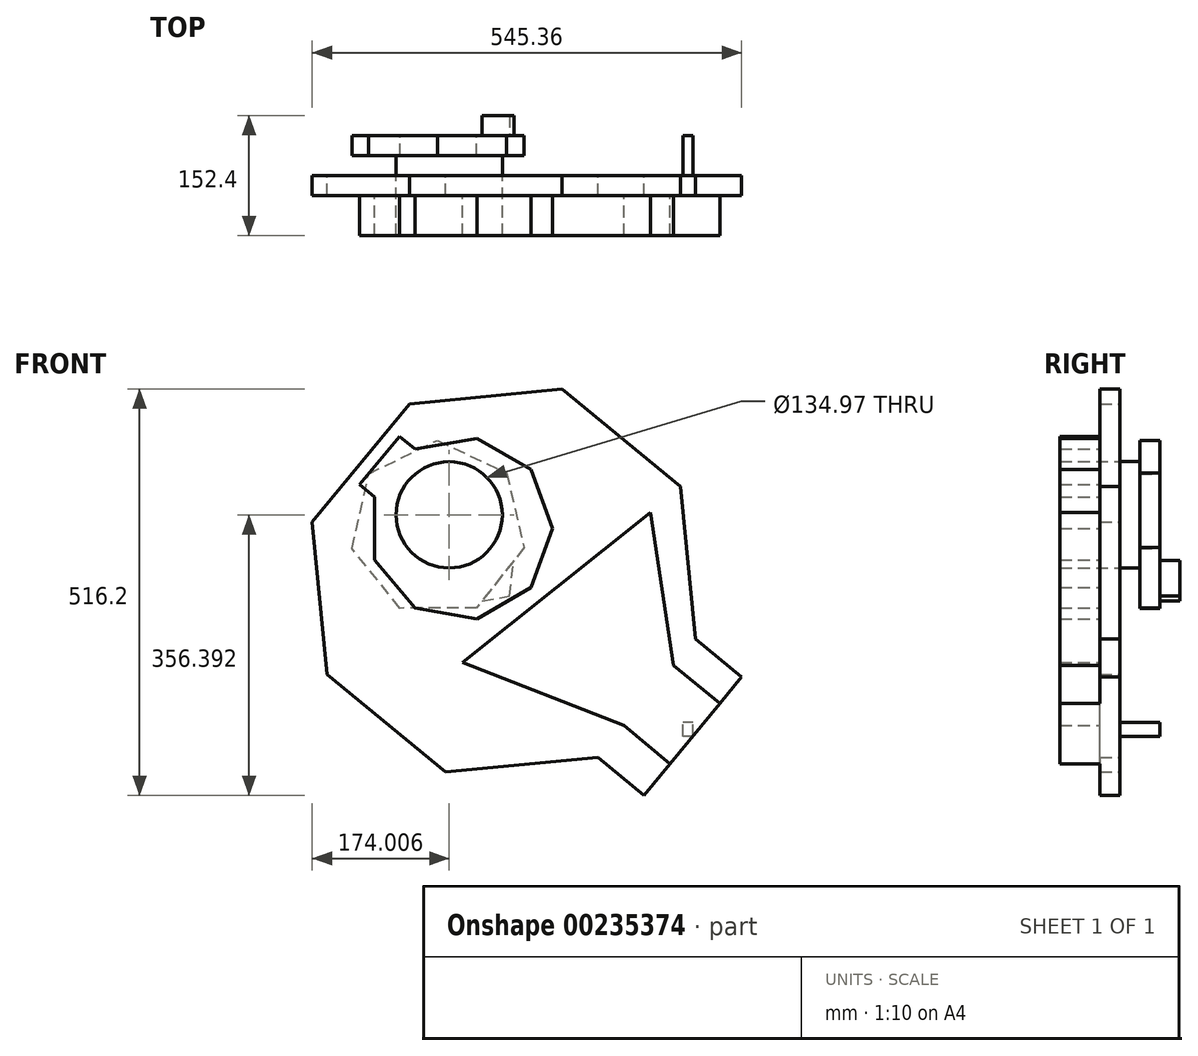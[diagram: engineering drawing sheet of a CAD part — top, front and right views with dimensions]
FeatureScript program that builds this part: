
annotation { "Feature Type Name" : "Feature", "Feature Type Description" : "" }
export const myFeature = defineFeature(function(context is Context, id is Id, definition is map)
    precondition{}
    {
        {
            var Q0;
            Q0=qCreatedBy(makeId("Front.planeOp"),FACE);
            var sketch = newSketch(context, id + "F0", { "sketchPlane" : qUnion([Q0])});
            skLineSegment(sketch, "E0.bottom", {"start": v(0, 0) * mm, "end": v(42.08, 0) * mm});
            skLineSegment(sketch, "E0.top", {"start": v(0, 55.56) * mm, "end": v(42.08, 55.56) * mm});
            skLineSegment(sketch, "E0.left", {"start": v(0, 0) * mm, "end": v(0, 55.56) * mm});
            skLineSegment(sketch, "E0.right", {"start": v(42.08, 0) * mm, "end": v(42.08, 55.56) * mm});
            skSolve(sketch);
        }
        {
            var Q0;
            Q0 = qSketchRegion(id + "F0", true);
            extrude(context, id + "F1", {"entities" : qUnion([Q0]), "depth" : 25.4 * mm});
        }
        {
            var Q0;
            Q0=makeQuery(id+"F1.opExtrude","CAP_FACE",FACE,{"disambiguationData":[OSD([sQuery(id+"F0.wireOp",EDGE,"E0.bottom"),sQuery(id+"F0.wireOp",EDGE,"E0.top"),sQuery(id+"F0.wireOp",EDGE,"E0.left"),sQuery(id+"F0.wireOp",EDGE,"E0.right")])],"isStart":false});
            var sketch = newSketch(context, id + "F2", { "sketchPlane" : qUnion([Q0])});
            skCircle(sketch, "E1", {"center": v(14.29, 17.4) * mm, "radius": 67.49 * mm});
            skSolve(sketch);
        }
        {
            var Q0;
            Q0 = qSketchRegion(id + "F2", true);
            extrude(context, id + "F3", {"entities" : qUnion([Q0]), "operationType" : NewBodyOperationType.ADD, "depth" : 25.4 * mm});
        }
        {
            var Q0;
            Q0=qCreatedBy(makeId("Front.planeOp"),FACE);
            var sketch = newSketch(context, id + "F4", { "sketchPlane" : qUnion([Q0])});
            skCircle(sketch, "E2.cCircle", {"center": v(0, 0) * mm, "radius": 100.97 * mm, "construction": true});
            skLineSegment(sketch, "E2.0", {"start": v(-48.02, -101.27) * mm, "end": v(-109.11, -25.6) * mm});
            skLineSegment(sketch, "E2.1", {"start": v(-109.11, -25.6) * mm, "end": v(-88.04, 69.35) * mm});
            skLineSegment(sketch, "E2.2", {"start": v(-88.04, 69.35) * mm, "end": v(-0.68, 112.07) * mm});
            skLineSegment(sketch, "E2.3", {"start": v(-0.68, 112.07) * mm, "end": v(87.2, 70.4) * mm});
            skLineSegment(sketch, "E2.4", {"start": v(87.2, 70.4) * mm, "end": v(109.41, -24.28) * mm});
            skLineSegment(sketch, "E2.5", {"start": v(109.41, -24.28) * mm, "end": v(49.24, -100.68) * mm});
            skLineSegment(sketch, "E2.6", {"start": v(49.24, -100.68) * mm, "end": v(-48.02, -101.27) * mm});
            skPoint(sketch, "E2.0.midPoint", {"position": v(-78.56, -63.43) * mm});
            skSolve(sketch);
        }
        {
            var Q0;
            Q0=makeQuery(id+"F4.imprint","IMPRINT",FACE,{"disambiguationData":[TD([[makeQuery(id+"F4.imprint","IMPRINT",EDGE,{"derivedFrom":sQuery(id+"F4.wireOp",EDGE,"E2.0")}),-1.0]])]});
            extrude(context, id + "F5", {"entities" : qUnion([Q0]), "operationType" : NewBodyOperationType.ADD, "depth" : 25.4 * mm});
        }
        {
            var Q0;
            Q0=makeQuery(id+"F3.opExtrude","CAP_FACE",FACE,{"disambiguationData":[OSD([sQuery(id+"F2.wireOp",EDGE,"E1")])],"isStart":false});
            var sketch = newSketch(context, id + "F6", { "sketchPlane" : qUnion([Q0])});
            skCircle(sketch, "E3.cCircle", {"center": v(83.55, -66.06) * mm, "radius": 234.98 * mm, "construction": true});
            skLineSegment(sketch, "E3.0", {"start": v(-35.98, 158.44) * mm, "end": v(157.78, 177.2) * mm});
            skLineSegment(sketch, "E3.1", {"start": v(157.78, 177.2) * mm, "end": v(308.05, 53.46) * mm});
            skLineSegment(sketch, "E3.2", {"start": v(308.05, 53.46) * mm, "end": v(326.81, -140.3) * mm});
            skLineSegment(sketch, "E3.3", {"start": v(326.81, -140.3) * mm, "end": v(203.07, -290.57) * mm});
            skLineSegment(sketch, "E3.4", {"start": v(203.07, -290.57) * mm, "end": v(9.32, -309.33) * mm});
            skLineSegment(sketch, "E3.5", {"start": v(9.32, -309.33) * mm, "end": v(-140.96, -185.58) * mm});
            skLineSegment(sketch, "E3.6", {"start": v(-140.96, -185.58) * mm, "end": v(-159.72, 8.17) * mm});
            skLineSegment(sketch, "E3.7", {"start": v(-159.72, 8.17) * mm, "end": v(-35.98, 158.44) * mm});
            skPoint(sketch, "E3.0.midPoint", {"position": v(60.9, 167.82) * mm});
            skSolve(sketch);
        }
        {
            var Q0;
            Q0=makeQuery(id+"F6.imprint","IMPRINT",FACE,{"disambiguationData":[TD([[makeQuery(id+"F6.imprint","IMPRINT",EDGE,{"derivedFrom":sQuery(id+"F6.wireOp",EDGE,"E3.0")}),-1.0]])]});
            extrude(context, id + "F7", {"entities" : qUnion([Q0]), "depth" : 25.4 * mm});
        }
        {
            var Q0;
            Q0=makeQuery(id+"F7.opExtrude","CAP_FACE",FACE,{"disambiguationData":[OSD([sQuery(id+"F2.wireOp",EDGE,"E1"),sQuery(id+"F6.wireOp",EDGE,"E3.0"),sQuery(id+"F6.wireOp",EDGE,"E3.1"),sQuery(id+"F6.wireOp",EDGE,"E3.2"),sQuery(id+"F6.wireOp",EDGE,"E3.3"),sQuery(id+"F6.wireOp",EDGE,"E3.4"),sQuery(id+"F6.wireOp",EDGE,"E3.5"),sQuery(id+"F6.wireOp",EDGE,"E3.6"),sQuery(id+"F6.wireOp",EDGE,"E3.7")])],"isStart":false});
            var sketch = newSketch(context, id + "F8", { "sketchPlane" : qUnion([Q0])});
            skCircle(sketch, "E4.cCircle", {"center": v(205.53, -143.68) * mm, "radius": 176.31 * mm, "construction": true});
            skLineSegment(sketch, "E4.0", {"start": v(315.67, -281.36) * mm, "end": v(31.23, -170.23) * mm});
            skLineSegment(sketch, "E4.1", {"start": v(31.23, -170.23) * mm, "end": v(269.7, 20.54) * mm});
            skLineSegment(sketch, "E4.2", {"start": v(269.7, 20.54) * mm, "end": v(315.67, -281.36) * mm});
            skSolve(sketch);
        }
        {
            var Q0;
            {var subQ0=sQuery(id+"F8.wireOp",EDGE,"E4.1");Q0=makeQuery(id+"F8.imprint","IMPRINT",FACE,{"disambiguationData":[TD([[makeQuery(id+"F8.imprint","IMPRINT",EDGE,{"derivedFrom":subQ0}),-1.0]])]});}
            extrude(context, id + "F9", {"entities" : qUnion([Q0]), "operationType" : NewBodyOperationType.ADD, "depth" : 25.4 * mm});
        }
        {
            var Q0;
            Q0=makeQuery(id+"F7.opExtrude","CAP_FACE",FACE,{"disambiguationData":[OSD([sQuery(id+"F2.wireOp",EDGE,"E1"),sQuery(id+"F6.wireOp",EDGE,"E3.0"),sQuery(id+"F6.wireOp",EDGE,"E3.1"),sQuery(id+"F6.wireOp",EDGE,"E3.2"),sQuery(id+"F6.wireOp",EDGE,"E3.3"),sQuery(id+"F6.wireOp",EDGE,"E3.4"),sQuery(id+"F6.wireOp",EDGE,"E3.5"),sQuery(id+"F6.wireOp",EDGE,"E3.6"),sQuery(id+"F6.wireOp",EDGE,"E3.7")])],"isStart":false});
            var sketch = newSketch(context, id + "F10", { "sketchPlane" : qUnion([Q0])});
            skCircle(sketch, "E5.cCircle", {"center": v(29.15, 0) * mm, "radius": 109.38 * mm, "construction": true});
            skLineSegment(sketch, "E5.0", {"start": v(-80.23, -39.81) * mm, "end": v(-80.23, 39.81) * mm});
            skLineSegment(sketch, "E5.1", {"start": v(-80.23, 39.81) * mm, "end": v(-29.05, 100.8) * mm});
            skLineSegment(sketch, "E5.2", {"start": v(-29.05, 100.8) * mm, "end": v(49.36, 114.63) * mm});
            skLineSegment(sketch, "E5.3", {"start": v(49.36, 114.63) * mm, "end": v(118.31, 74.82) * mm});
            skLineSegment(sketch, "E5.4", {"start": v(118.31, 74.82) * mm, "end": v(145.55, 0) * mm});
            skLineSegment(sketch, "E5.5", {"start": v(145.55, 0) * mm, "end": v(118.31, -74.82) * mm});
            skLineSegment(sketch, "E5.6", {"start": v(118.31, -74.82) * mm, "end": v(49.36, -114.63) * mm});
            skLineSegment(sketch, "E5.7", {"start": v(49.36, -114.63) * mm, "end": v(-29.05, -100.8) * mm});
            skLineSegment(sketch, "E5.8", {"start": v(-29.05, -100.8) * mm, "end": v(-80.23, -39.81) * mm});
            skPoint(sketch, "E5.0.midPoint", {"position": v(-80.23, 0) * mm});
            skSolve(sketch);
        }
        {
            var Q0;
            Q0=makeQuery(id+"F10.imprint","IMPRINT",FACE,{"disambiguationData":[TD([[makeQuery(id+"F10.imprint","IMPRINT",EDGE,{"derivedFrom":sQuery(id+"F10.wireOp",EDGE,"E5.0")}),-1.0]])]});
            extrude(context, id + "F11", {"entities" : qUnion([Q0]), "operationType" : NewBodyOperationType.ADD, "depth" : 25.4 * mm});
        }
        {
            var Q0;
            Q0=makeQuery(id+"F11.opExtrude","SWEPT_FACE",FACE,{"disambiguationData":[OSD([sQuery(id+"F10.wireOp",EDGE,"E5.1")])]});
            extrude(context, id + "F12", {"entities" : qUnion([Q0]), "operationType" : NewBodyOperationType.ADD, "depth" : 25.4 * mm});
        }
        {
            var Q0;
            {var subQ0=sQuery(id+"F10.wireOp",EDGE,"E5.1");Q0=makeQuery(id+"F12.boolean.opBoolean","MERGE",FACE,{"derivedFrom":[makeQuery(id+"F11.opExtrude","CAP_FACE",FACE,{"disambiguationData":[OSD([sQuery(id+"F2.wireOp",EDGE,"E1"),sQuery(id+"F10.wireOp",EDGE,"E5.0"),subQ0,sQuery(id+"F10.wireOp",EDGE,"E5.2"),sQuery(id+"F10.wireOp",EDGE,"E5.3"),sQuery(id+"F10.wireOp",EDGE,"E5.4"),sQuery(id+"F10.wireOp",EDGE,"E5.5"),sQuery(id+"F10.wireOp",EDGE,"E5.6"),sQuery(id+"F10.wireOp",EDGE,"E5.7"),sQuery(id+"F10.wireOp",EDGE,"E5.8")])],"isStart":false}),makeQuery(id+"F12.opExtrude","SWEPT_FACE",FACE,{"disambiguationData":[OSD([subQ0]),TDD([makeQuery(id+"F11.opExtrude","CAP_EDGE",EDGE,{"disambiguationData":[OSD([subQ0])],"isStart":false})])]})]});}
            var Q1;
            Q1=makeQuery(id+"F9.opExtrude","CAP_FACE",FACE,{"disambiguationData":[OSD([sQuery(id+"F6.wireOp",EDGE,"E3.3"),sQuery(id+"F8.wireOp",EDGE,"E4.0"),sQuery(id+"F8.wireOp",EDGE,"E4.1"),sQuery(id+"F8.wireOp",EDGE,"E4.2")])],"isStart":false});
            extrude(context, id + "F13", {"entities" : qUnion([Q0, Q1]), "operationType" : NewBodyOperationType.ADD, "depth" : 25.4 * mm});
        }
        {
            var Q0;
            {var subQ0=sQuery(id+"F6.wireOp",EDGE,"E3.3");Q0=makeQuery(id+"F13.boolean.opBoolean","MERGE",FACE,{"derivedFrom":[makeQuery(id+"F9.boolean.opBoolean","MERGE",FACE,{"derivedFrom":[makeQuery(id+"F7.opExtrude","SWEPT_FACE",FACE,{"disambiguationData":[OSD([subQ0])]}),makeQuery(id+"F9.opExtrude","SWEPT_FACE",FACE,{"disambiguationData":[OSD([subQ0])]})]}),makeQuery(id+"F13.opExtrude","SWEPT_FACE",FACE,{"disambiguationData":[OSD([subQ0])]})]});}
            extrude(context, id + "F14", {"entities" : qUnion([Q0]), "operationType" : NewBodyOperationType.ADD, "depth" : 25.4 * mm});
        }
        {
            var Q0;
            Q0=makeQuery(id+"F14.opExtrude","CAP_FACE",FACE,{"disambiguationData":[OSD([sQuery(id+"F6.wireOp",EDGE,"E3.3")])],"isStart":false});
            extrude(context, id + "F15", {"entities" : qUnion([Q0]), "operationType" : NewBodyOperationType.ADD, "depth" : 25.4 * mm});
        }
        {
            var Q0;
            Q0=makeQuery(id+"F15.opExtrude","CAP_FACE",FACE,{"disambiguationData":[OSD([sQuery(id+"F6.wireOp",EDGE,"E3.3")])],"isStart":false});
            extrude(context, id + "F16", {"entities" : qUnion([Q0]), "operationType" : NewBodyOperationType.ADD, "depth" : 25.4 * mm});
        }
        {
            var Q0;
            {var subQ0=sQuery(id+"F6.wireOp",EDGE,"E3.3");var subQ1=makeQuery(id+"F7.opExtrude","CAP_EDGE",EDGE,{"disambiguationData":[OSD([subQ0])],"isStart":true});var subQ2=makeQuery(id+"F14.opExtrude","CAP_EDGE",EDGE,{"disambiguationData":[OSD([subQ0]),TDD([subQ1])],"isStart":false});Q0=makeQuery(id+"F16.boolean.opBoolean","MERGE",FACE,{"derivedFrom":[makeQuery(id+"F15.boolean.opBoolean","MERGE",FACE,{"derivedFrom":[makeQuery(id+"F14.boolean.opBoolean","MERGE",FACE,{"derivedFrom":[makeQuery(id+"F7.opExtrude","CAP_FACE",FACE,{"disambiguationData":[OSD([sQuery(id+"F2.wireOp",EDGE,"E1"),sQuery(id+"F6.wireOp",EDGE,"E3.0"),sQuery(id+"F6.wireOp",EDGE,"E3.1"),sQuery(id+"F6.wireOp",EDGE,"E3.2"),subQ0,sQuery(id+"F6.wireOp",EDGE,"E3.4"),sQuery(id+"F6.wireOp",EDGE,"E3.5"),sQuery(id+"F6.wireOp",EDGE,"E3.6"),sQuery(id+"F6.wireOp",EDGE,"E3.7")])],"isStart":true}),makeQuery(id+"F14.opExtrude","SWEPT_FACE",FACE,{"disambiguationData":[OSD([subQ0]),TDD([subQ1])]})]}),makeQuery(id+"F15.opExtrude","SWEPT_FACE",FACE,{"disambiguationData":[OSD([subQ0]),TDD([subQ2])]})]}),makeQuery(id+"F16.opExtrude","SWEPT_FACE",FACE,{"disambiguationData":[OSD([subQ0]),TDD([makeQuery(id+"F15.opExtrude","CAP_EDGE",EDGE,{"disambiguationData":[OSD([subQ0]),TDD([subQ2])],"isStart":false})])]})]});}
            var sketch = newSketch(context, id + "F17", { "sketchPlane" : qUnion([Q0])});
            skLineSegment(sketch, "E6.bottom", {"start": v(-323.77, -263.87) * mm, "end": v(-311.1, -263.87) * mm});
            skLineSegment(sketch, "E6.top", {"start": v(-323.77, -246.54) * mm, "end": v(-311.1, -246.54) * mm});
            skLineSegment(sketch, "E6.left", {"start": v(-323.77, -263.87) * mm, "end": v(-323.77, -246.54) * mm});
            skLineSegment(sketch, "E6.right", {"start": v(-311.1, -263.87) * mm, "end": v(-311.1, -246.54) * mm});
            skSolve(sketch);
        }
        {
            var Q0;
            Q0=makeQuery(id+"F17.imprint","IMPRINT",FACE,{"disambiguationData":[TD([[makeQuery(id+"F17.imprint","IMPRINT",EDGE,{"derivedFrom":sQuery(id+"F17.wireOp",EDGE,"E6.bottom")}),1.0]])]});
            extrude(context, id + "F18", {"entities" : qUnion([Q0]), "operationType" : NewBodyOperationType.ADD, "depth" : 25.4 * mm});
        }
        {
            var Q0;
            Q0=makeQuery(id+"F18.opExtrude","CAP_FACE",FACE,{"disambiguationData":[OSD([sQuery(id+"F17.wireOp",EDGE,"E6.bottom"),sQuery(id+"F17.wireOp",EDGE,"E6.top"),sQuery(id+"F17.wireOp",EDGE,"E6.left"),sQuery(id+"F17.wireOp",EDGE,"E6.right")])],"isStart":false});
            extrude(context, id + "F19", {"entities" : qUnion([Q0]), "operationType" : NewBodyOperationType.ADD, "depth" : 25.4 * mm});
        }
        {
            var Q0;
            Q0=makeQuery(id+"F19.opExtrude","CAP_FACE",FACE,{"disambiguationData":[OSD([sQuery(id+"F17.wireOp",EDGE,"E6.bottom"),sQuery(id+"F17.wireOp",EDGE,"E6.top"),sQuery(id+"F17.wireOp",EDGE,"E6.left"),sQuery(id+"F17.wireOp",EDGE,"E6.right")])],"isStart":false});
            extrude(context, id + "F20", {"entities" : qUnion([Q0]), "operationType" : NewBodyOperationType.ADD, "oppositeDirection" : true, "depth" : 25.4 * mm});
        }
        {
            var Q0;
            Q0=makeQuery(id+"F5.boolean.opBoolean","MERGE",FACE,{"derivedFrom":[makeQuery(id+"F1.opExtrude","CAP_FACE",FACE,{"disambiguationData":[OSD([sQuery(id+"F0.wireOp",EDGE,"E0.bottom"),sQuery(id+"F0.wireOp",EDGE,"E0.top"),sQuery(id+"F0.wireOp",EDGE,"E0.left"),sQuery(id+"F0.wireOp",EDGE,"E0.right")])],"isStart":true}),makeQuery(id+"F5.opExtrude","CAP_FACE",FACE,{"disambiguationData":[OSD([sQuery(id+"F4.wireOp",EDGE,"E2.0"),sQuery(id+"F4.wireOp",EDGE,"E2.1"),sQuery(id+"F4.wireOp",EDGE,"E2.2"),sQuery(id+"F4.wireOp",EDGE,"E2.3"),sQuery(id+"F4.wireOp",EDGE,"E2.4"),sQuery(id+"F4.wireOp",EDGE,"E2.5"),sQuery(id+"F4.wireOp",EDGE,"E2.6")])],"isStart":true})]});
            var sketch = newSketch(context, id + "F21", { "sketchPlane" : qUnion([Q0])});
            skCircle(sketch, "E7.cCircle", {"center": v(0, 0) * mm, "radius": 100.97 * mm, "construction": true});
            skLineSegment(sketch, "E7.0", {"start": v(-109.55, 59.8) * mm, "end": v(23.03, 122.67) * mm});
            skLineSegment(sketch, "E7.1", {"start": v(23.03, 122.67) * mm, "end": v(123.78, 16) * mm});
            skLineSegment(sketch, "E7.2", {"start": v(123.78, 16) * mm, "end": v(53.47, -112.78) * mm});
            skLineSegment(sketch, "E7.3", {"start": v(53.47, -112.78) * mm, "end": v(-90.73, -85.7) * mm});
            skLineSegment(sketch, "E7.4", {"start": v(-90.73, -85.7) * mm, "end": v(-109.55, 59.8) * mm});
            skPoint(sketch, "E7.0.midPoint", {"position": v(-43.26, 91.24) * mm});
            skSolve(sketch);
        }
        {
            var Q0;
            {var subQ0=sQuery(id+"F21.wireOp",EDGE,"E7.4");var subQ1=sQuery(id+"F21.wireOp",EDGE,"E7.3");var subQ2=makeQuery(id+"F21.imprint","INTERSECT",VERTEX,{"derivedFrom":[subQ1,subQ0]});Q0=makeQuery(id+"F21.imprint","IMPRINT",FACE,{"disambiguationData":[TD([[makeQuery(id+"F21.imprint","IMPRINT",EDGE,{"disambiguationData":[TD([[subQ2,1.0]])],"derivedFrom":subQ1}),-1.0]])]});}
            extrude(context, id + "F22", {"entities" : qUnion([Q0]), "depth" : 25.4 * mm});
        }
    });
